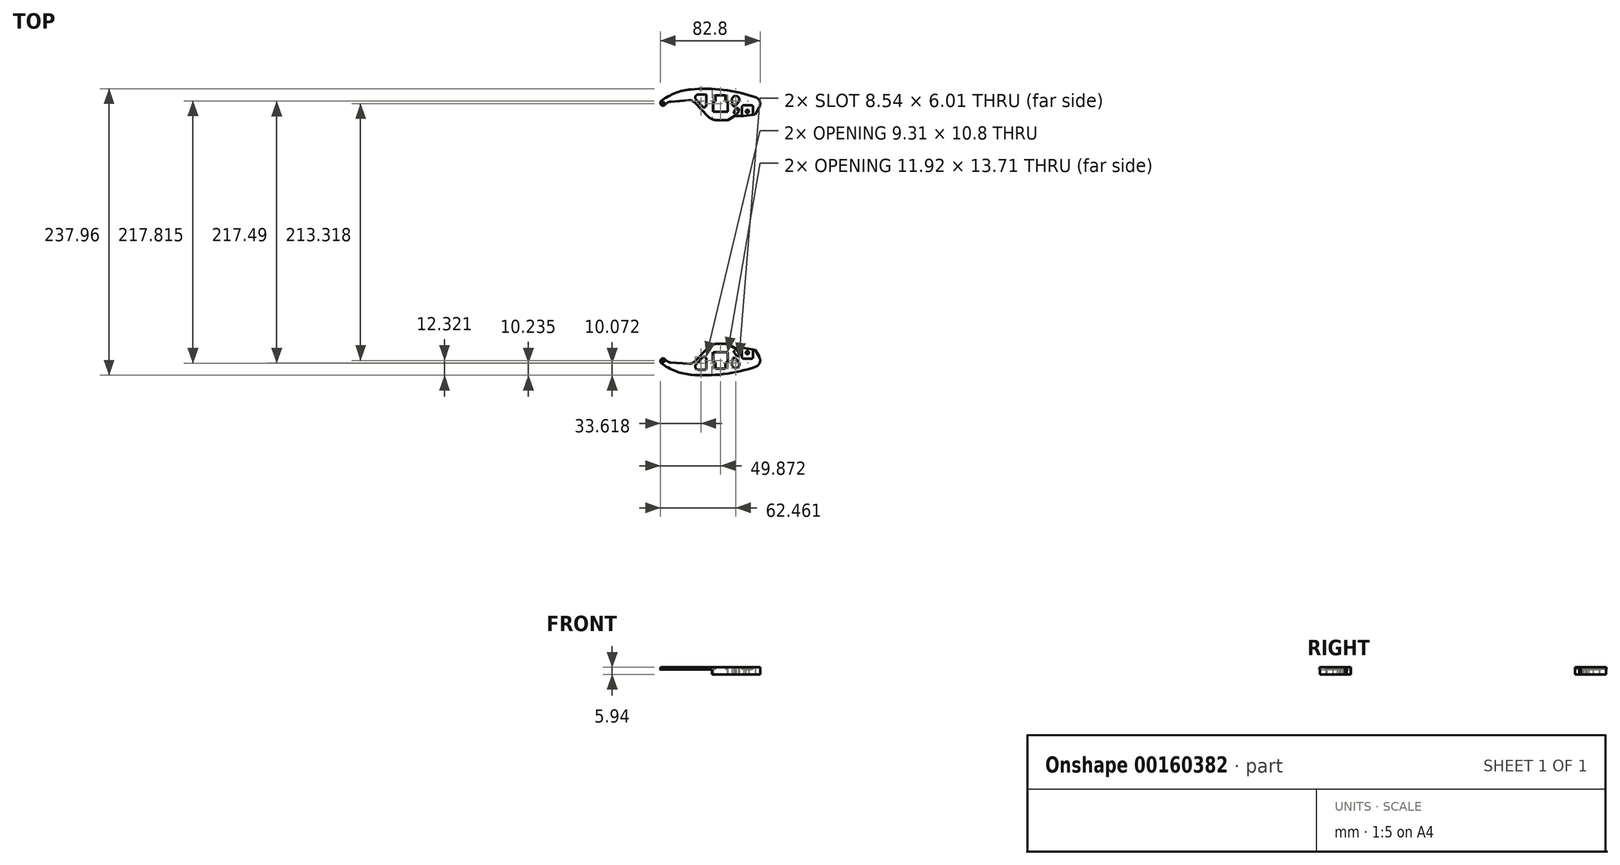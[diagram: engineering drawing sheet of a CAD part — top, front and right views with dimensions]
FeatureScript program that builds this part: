
annotation { "Feature Type Name" : "Feature", "Feature Type Description" : "" }
export const myFeature = defineFeature(function(context is Context, id is Id, definition is map)
    precondition{}
    {
        {
            var Q0;
            Q0=qCreatedBy(makeId("Top.planeOp"),FACE);
            var sketch = newSketch(context, id + "F0", { "sketchPlane" : qUnion([Q0])});
            skLineSegment(sketch, "E0", {"start": v(-38.77, 92.9) * mm, "end": v(-48, 92.9) * mm});
            skArc(sketch, "E1", {"start": v(-48, 92.9) * mm, "mid": v(-51.77, 93.67) * mm, "end": v(-54.94, 95.84) * mm});
            skLineSegment(sketch, "E2", {"start": v(-54.94, 95.84) * mm, "end": v(-66.16, 107.4) * mm});
            skArc(sketch, "E3", {"start": v(-66.16, 107.4) * mm, "mid": v(-68.67, 109.05) * mm, "end": v(-71.65, 109.47) * mm});
            skLineSegment(sketch, "E4", {"start": v(-71.65, 109.47) * mm, "end": v(-86.34, 108.3) * mm});
            skArc(sketch, "E5", {"start": v(-86.34, 108.3) * mm, "mid": v(-88.83, 107.55) * mm, "end": v(-90.8, 105.86) * mm});
            skArc(sketch, "E6", {"start": v(-90.8, 105.86) * mm, "mid": v(-94.13, 105.64) * mm, "end": v(-93.92, 108.96) * mm});
            skArc(sketch, "E7", {"start": v(-69.69, 118.46) * mm, "mid": v(-82.47, 115.43) * mm, "end": v(-93.92, 108.96) * mm});
            skArc(sketch, "E8", {"start": v(-15.82, 111.92) * mm, "mid": v(-42.4, 118.03) * mm, "end": v(-69.69, 118.46) * mm});
            skArc(sketch, "E9", {"start": v(-12.64, 103.92) * mm, "mid": v(-12.39, 108.65) * mm, "end": v(-15.82, 111.92) * mm});
            skLineSegment(sketch, "E10", {"start": v(-12.64, 103.92) * mm, "end": v(-15.88, 97.74) * mm});
            skLineSegment(sketch, "E11", {"start": v(-15.88, 97.74) * mm, "end": v(-25.7, 96.38) * mm});
            skLineSegment(sketch, "E12", {"start": v(-25.7, 96.38) * mm, "end": v(-33.28, 96.38) * mm});
            skLineSegment(sketch, "E13", {"start": v(-33.28, 96.38) * mm, "end": v(-38.77, 92.9) * mm});
            skCircle(sketch, "E14", {"center": v(-32.29, 110) * mm, "radius": 3.05 * mm});
            skCircle(sketch, "E15", {"center": v(-33.62, 105.82) * mm, "radius": 1.35 * mm});
            skLineSegment(sketch, "E16", {"start": v(-35.32, 109.73) * mm, "end": v(-34.96, 105.7) * mm});
            skLineSegment(sketch, "E17", {"start": v(-29.81, 108.23) * mm, "end": v(-32.59, 104.95) * mm});
            skCircle(sketch, "E18", {"center": v(-30.89, 101.86) * mm, "radius": 1.08 * mm});
            skCircle(sketch, "E19", {"center": v(-30.6, 100.02) * mm, "radius": 0.75 * mm});
            skCircle(sketch, "E20", {"center": v(-32.75, 99.4) * mm, "radius": 1.08 * mm});
            skCircle(sketch, "E21", {"center": v(-31.77, 98.94) * mm, "radius": 0.7 * mm});
            skLineSegment(sketch, "E22", {"start": v(-32.97, 98.34) * mm, "end": v(-31.82, 98.25) * mm});
            skLineSegment(sketch, "E23", {"start": v(-31.32, 98.42) * mm, "end": v(-30.1, 99.45) * mm});
            skLineSegment(sketch, "E24", {"start": v(-29.85, 100.12) * mm, "end": v(-29.8, 101.83) * mm});
            skLineSegment(sketch, "E25", {"start": v(-31.73, 102.54) * mm, "end": v(-33.61, 100.05) * mm});
            skLineSegment(sketch, "E26.bottom", {"start": v(-38.95, 108.35) * mm, "end": v(-50.87, 108.35) * mm});
            skLineSegment(sketch, "E26.top", {"start": v(-38.95, 99.8) * mm, "end": v(-50.87, 99.8) * mm});
            skLineSegment(sketch, "E26.left", {"start": v(-38.95, 108.35) * mm, "end": v(-38.95, 99.8) * mm});
            skLineSegment(sketch, "E26.right", {"start": v(-50.87, 108.35) * mm, "end": v(-50.87, 99.8) * mm});
            skLineSegment(sketch, "E27.bottom", {"start": v(-40.93, 113.51) * mm, "end": v(-49.08, 113.51) * mm});
            skLineSegment(sketch, "E27.top", {"start": v(-40.93, 108.35) * mm, "end": v(-49.08, 108.35) * mm});
            skLineSegment(sketch, "E27.left", {"start": v(-40.93, 113.51) * mm, "end": v(-40.93, 108.35) * mm});
            skLineSegment(sketch, "E27.right", {"start": v(-49.08, 113.51) * mm, "end": v(-49.08, 108.35) * mm});
            skLineSegment(sketch, "E28", {"start": v(-56.5, 113.04) * mm, "end": v(-56.5, 105.52) * mm});
            skLineSegment(sketch, "E29", {"start": v(-56.84, 104.67) * mm, "end": v(-57.51, 103.92) * mm});
            skLineSegment(sketch, "E30", {"start": v(-59.38, 103.9) * mm, "end": v(-64.82, 109.63) * mm});
            skLineSegment(sketch, "E31", {"start": v(-57.78, 114.3) * mm, "end": v(-63.2, 114.3) * mm});
            skArc(sketch, "E32", {"start": v(-63.2, 114.3) * mm, "mid": v(-65.67, 112.55) * mm, "end": v(-64.82, 109.63) * mm});
            skPoint(sketch, "E33.visualSharp", {"position": v(-56.5, 114.3) * mm});
            skArc(sketch, "E33.filletArc", {"start": v(-56.5, 113.04) * mm, "mid": v(-56.88, 113.94) * mm, "end": v(-57.78, 114.3) * mm});
            skPoint(sketch, "E34.visualSharp", {"position": v(-58.43, 102.9) * mm});
            skArc(sketch, "E34.filletArc", {"start": v(-59.38, 103.9) * mm, "mid": v(-58.44, 103.5) * mm, "end": v(-57.51, 103.92) * mm});
            skPoint(sketch, "E35.visualSharp", {"position": v(-56.5, 105.04) * mm});
            skArc(sketch, "E35.filletArc", {"start": v(-56.84, 104.67) * mm, "mid": v(-56.6, 105.07) * mm, "end": v(-56.5, 105.52) * mm});
            skCircle(sketch, "E36", {"center": v(-92.57, 107.2) * mm, "radius": 0.95 * mm});
            skCircle(sketch, "E37", {"center": v(-22.58, 100.2) * mm, "radius": 1.27 * mm});
            skSolve(sketch);
        }
        {
            var Q0;
            Q0 = qSketchRegion(id + "F0", true);
            extrude(context, id + "F1", {"entities" : qUnion([Q0]), "depth" : 1.98 * mm});
        }
        {
            var Q0;
            Q0=makeQuery(id+"F1.opExtrude","CAP_FACE",FACE,{"disambiguationData":[OSD([sQuery(id+"F0.wireOp",EDGE,"E0"),sQuery(id+"F0.wireOp",EDGE,"E1"),sQuery(id+"F0.wireOp",EDGE,"E2"),sQuery(id+"F0.wireOp",EDGE,"E3"),sQuery(id+"F0.wireOp",EDGE,"E4"),sQuery(id+"F0.wireOp",EDGE,"E5"),sQuery(id+"F0.wireOp",EDGE,"E6"),sQuery(id+"F0.wireOp",EDGE,"E7"),sQuery(id+"F0.wireOp",EDGE,"E8"),sQuery(id+"F0.wireOp",EDGE,"E9"),sQuery(id+"F0.wireOp",EDGE,"E10"),sQuery(id+"F0.wireOp",EDGE,"E11"),sQuery(id+"F0.wireOp",EDGE,"E12"),sQuery(id+"F0.wireOp",EDGE,"E13"),sQuery(id+"F0.wireOp",EDGE,"E14"),sQuery(id+"F0.wireOp",EDGE,"E15"),sQuery(id+"F0.wireOp",EDGE,"E16"),sQuery(id+"F0.wireOp",EDGE,"E17"),sQuery(id+"F0.wireOp",EDGE,"E18"),sQuery(id+"F0.wireOp",EDGE,"E19"),sQuery(id+"F0.wireOp",EDGE,"E20"),sQuery(id+"F0.wireOp",EDGE,"E21"),sQuery(id+"F0.wireOp",EDGE,"E22"),sQuery(id+"F0.wireOp",EDGE,"E23"),sQuery(id+"F0.wireOp",EDGE,"E24"),sQuery(id+"F0.wireOp",EDGE,"E25"),sQuery(id+"F0.wireOp",EDGE,"E26.bottom"),sQuery(id+"F0.wireOp",EDGE,"E26.top"),sQuery(id+"F0.wireOp",EDGE,"E26.left"),sQuery(id+"F0.wireOp",EDGE,"E26.right"),sQuery(id+"F0.wireOp",EDGE,"E27.bottom"),sQuery(id+"F0.wireOp",EDGE,"E27.left"),sQuery(id+"F0.wireOp",EDGE,"E27.right"),sQuery(id+"F0.wireOp",EDGE,"E28"),sQuery(id+"F0.wireOp",EDGE,"E29"),sQuery(id+"F0.wireOp",EDGE,"E30"),sQuery(id+"F0.wireOp",EDGE,"E31"),sQuery(id+"F0.wireOp",EDGE,"E32"),sQuery(id+"F0.wireOp",EDGE,"E33.filletArc"),sQuery(id+"F0.wireOp",EDGE,"E34.filletArc"),sQuery(id+"F0.wireOp",EDGE,"E35.filletArc"),sQuery(id+"F0.wireOp",EDGE,"E36"),sQuery(id+"F0.wireOp",EDGE,"E37")])],"isStart":true});
            var sketch = newSketch(context, id + "F2", { "sketchPlane" : qUnion([Q0])});
            skArc(sketch, "E38.0", {"start": v(-30.13, -107.86) * mm, "mid": v(-31.26, -112.87) * mm, "end": v(-35.32, -109.73) * mm});
            skLineSegment(sketch, "E38.1", {"start": v(-30.13, -107.86) * mm, "end": v(-32.59, -104.95) * mm});
            skArc(sketch, "E38.2", {"start": v(-34.96, -105.7) * mm, "mid": v(-34.02, -104.54) * mm, "end": v(-32.59, -104.95) * mm});
            skLineSegment(sketch, "E38.3", {"start": v(-35.32, -109.73) * mm, "end": v(-34.96, -105.7) * mm});
            skLineSegment(sketch, "E38.4", {"start": v(-31.77, -102.48) * mm, "end": v(-33.61, -100.05) * mm});
            skArc(sketch, "E38.5", {"start": v(-29.8, -101.83) * mm, "mid": v(-30.55, -102.88) * mm, "end": v(-31.77, -102.48) * mm});
            skLineSegment(sketch, "E38.6", {"start": v(-29.85, -100.12) * mm, "end": v(-29.8, -101.83) * mm});
            skPoint(sketch, "E38.7", {"position": v(-29.85, -100.12) * mm});
            skPoint(sketch, "E38.8", {"position": v(-31.32, -98.42) * mm});
            skArc(sketch, "E38.9", {"start": v(-30.1, -99.45) * mm, "mid": v(-29.9, -99.75) * mm, "end": v(-29.85, -100.12) * mm});
            skLineSegment(sketch, "E38.10", {"start": v(-31.32, -98.42) * mm, "end": v(-30.1, -99.45) * mm});
            skArc(sketch, "E38.11", {"start": v(-31.82, -98.25) * mm, "mid": v(-31.55, -98.29) * mm, "end": v(-31.32, -98.42) * mm});
            skLineSegment(sketch, "E38.12", {"start": v(-32.7, -98.32) * mm, "end": v(-31.82, -98.25) * mm});
            skArc(sketch, "E38.13", {"start": v(-33.61, -100.05) * mm, "mid": v(-33.7, -98.89) * mm, "end": v(-32.7, -98.32) * mm});
            skCircle(sketch, "E38.14", {"center": v(-22.58, -100.2) * mm, "radius": 1.27 * mm});
            skLineSegment(sketch, "E38.15", {"start": v(-12.64, -103.92) * mm, "end": v(-15.88, -97.74) * mm});
            skArc(sketch, "E38.16", {"start": v(-12.64, -103.92) * mm, "mid": v(-12.39, -108.65) * mm, "end": v(-15.82, -111.92) * mm});
            skArc(sketch, "E38.17", {"start": v(-15.82, -111.92) * mm, "mid": v(-33.6, -116.65) * mm, "end": v(-51.88, -118.83) * mm});
            skLineSegment(sketch, "E38.18", {"start": v(-25.7, -96.38) * mm, "end": v(-33.28, -96.38) * mm});
            skLineSegment(sketch, "E38.19", {"start": v(-15.88, -97.74) * mm, "end": v(-25.7, -96.38) * mm});
            skLineSegment(sketch, "E38.20", {"start": v(-33.28, -96.38) * mm, "end": v(-38.77, -92.9) * mm});
            skLineSegment(sketch, "E38.21", {"start": v(-38.77, -92.9) * mm, "end": v(-48, -92.9) * mm});
            skLineSegment(sketch, "E39", {"start": v(-55.8, -70.08) * mm, "end": v(-55.8, -80.65) * mm, "construction": true});
            skLineSegment(sketch, "E40", {"start": v(-56.81, -69.9) * mm, "end": v(-56.81, -80.65) * mm, "construction": true});
            skLineSegment(sketch, "E41.bottom", {"start": v(-38.95, -99.8) * mm, "end": v(-50.87, -99.8) * mm});
            skLineSegment(sketch, "E41.top", {"start": v(-38.95, -113.51) * mm, "end": v(-50.87, -113.51) * mm});
            skLineSegment(sketch, "E41.left", {"start": v(-38.95, -99.8) * mm, "end": v(-38.95, -113.51) * mm});
            skLineSegment(sketch, "E41.right", {"start": v(-50.87, -99.8) * mm, "end": v(-50.87, -113.51) * mm});
            skLineSegment(sketch, "E42", {"start": v(-51.88, -118.83) * mm, "end": v(-51.88, -93.72) * mm});
            skPoint(sketch, "E43.orphan", {"position": v(-69.69, -118.46) * mm});
            skArc(sketch, "E44", {"start": v(-48, -92.9) * mm, "mid": v(-49.98, -93.1) * mm, "end": v(-51.88, -93.72) * mm});
            skSolve(sketch);
        }
        {
            var Q0;
            Q0 = qSketchRegion(id + "F2", true);
            extrude(context, id + "F3", {"entities" : qUnion([Q0]), "operationType" : NewBodyOperationType.ADD, "depth" : 1.98 * mm * 2});
        }
        {
            var Q0;
            Q0=makeQuery(id+"F1.opExtrude","CAP_FACE",FACE,{"disambiguationData":[OSD([sQuery(id+"F0.wireOp",EDGE,"E0"),sQuery(id+"F0.wireOp",EDGE,"E1"),sQuery(id+"F0.wireOp",EDGE,"E2"),sQuery(id+"F0.wireOp",EDGE,"E3"),sQuery(id+"F0.wireOp",EDGE,"E4"),sQuery(id+"F0.wireOp",EDGE,"E5"),sQuery(id+"F0.wireOp",EDGE,"E6"),sQuery(id+"F0.wireOp",EDGE,"E7"),sQuery(id+"F0.wireOp",EDGE,"E8"),sQuery(id+"F0.wireOp",EDGE,"E9"),sQuery(id+"F0.wireOp",EDGE,"E10"),sQuery(id+"F0.wireOp",EDGE,"E11"),sQuery(id+"F0.wireOp",EDGE,"E12"),sQuery(id+"F0.wireOp",EDGE,"E13"),sQuery(id+"F0.wireOp",EDGE,"E14"),sQuery(id+"F0.wireOp",EDGE,"E15"),sQuery(id+"F0.wireOp",EDGE,"E16"),sQuery(id+"F0.wireOp",EDGE,"E17"),sQuery(id+"F0.wireOp",EDGE,"E18"),sQuery(id+"F0.wireOp",EDGE,"E19"),sQuery(id+"F0.wireOp",EDGE,"E20"),sQuery(id+"F0.wireOp",EDGE,"E21"),sQuery(id+"F0.wireOp",EDGE,"E22"),sQuery(id+"F0.wireOp",EDGE,"E23"),sQuery(id+"F0.wireOp",EDGE,"E24"),sQuery(id+"F0.wireOp",EDGE,"E25"),sQuery(id+"F0.wireOp",EDGE,"E26.bottom"),sQuery(id+"F0.wireOp",EDGE,"E26.top"),sQuery(id+"F0.wireOp",EDGE,"E26.left"),sQuery(id+"F0.wireOp",EDGE,"E26.right"),sQuery(id+"F0.wireOp",EDGE,"E27.bottom"),sQuery(id+"F0.wireOp",EDGE,"E27.left"),sQuery(id+"F0.wireOp",EDGE,"E27.right"),sQuery(id+"F0.wireOp",EDGE,"E28"),sQuery(id+"F0.wireOp",EDGE,"E29"),sQuery(id+"F0.wireOp",EDGE,"E30"),sQuery(id+"F0.wireOp",EDGE,"E31"),sQuery(id+"F0.wireOp",EDGE,"E32"),sQuery(id+"F0.wireOp",EDGE,"E33.filletArc"),sQuery(id+"F0.wireOp",EDGE,"E34.filletArc"),sQuery(id+"F0.wireOp",EDGE,"E35.filletArc"),sQuery(id+"F0.wireOp",EDGE,"E36"),sQuery(id+"F0.wireOp",EDGE,"E37")])],"isStart":false});
            var sketch = newSketch(context, id + "F4", { "sketchPlane" : qUnion([Q0])});
            skLineSegment(sketch, "E45.bottom", {"start": v(-27.06, 96.38) * mm, "end": v(-25.7, 96.38) * mm});
            skLineSegment(sketch, "E45.top", {"start": v(-25.8, 105.18) * mm, "end": v(-19.19, 105.18) * mm});
            skLineSegment(sketch, "E45.left", {"start": v(-27.06, 96.38) * mm, "end": v(-27.06, 103.91) * mm});
            skLineSegment(sketch, "E45.right", {"start": v(-17.92, 97.46) * mm, "end": v(-17.92, 103.91) * mm});
            skLineSegment(sketch, "E46.0", {"start": v(-17.92, 97.46) * mm, "end": v(-25.7, 96.38) * mm});
            skPoint(sketch, "E47.orphan", {"position": v(-15.88, 97.74) * mm});
            skPoint(sketch, "E48.visualSharp", {"position": v(-27.06, 105.18) * mm});
            skArc(sketch, "E48.filletArc", {"start": v(-25.8, 105.18) * mm, "mid": v(-26.69, 104.8) * mm, "end": v(-27.06, 103.91) * mm});
            skPoint(sketch, "E49.visualSharp", {"position": v(-17.92, 105.18) * mm});
            skArc(sketch, "E49.filletArc", {"start": v(-17.92, 103.91) * mm, "mid": v(-18.3, 104.8) * mm, "end": v(-19.19, 105.18) * mm});
            skSolve(sketch);
        }
        {
            var Q0;
            Q0 = qSketchRegion(id + "F4", true);
            extrude(context, id + "F5", {"entities" : qUnion([Q0]), "operationType" : NewBodyOperationType.REMOVE, "oppositeDirection" : true, "depth" : 1.98 * mm});
        }
        {
            var Q0;
            Q0=makeQuery(id+"F1.opExtrude","SWEPT_BODY",BODY,{"disambiguationData":[OSD([sQuery(id+"F0.wireOp",EDGE,"E0"),sQuery(id+"F0.wireOp",EDGE,"E1"),sQuery(id+"F0.wireOp",EDGE,"E2"),sQuery(id+"F0.wireOp",EDGE,"E3"),sQuery(id+"F0.wireOp",EDGE,"E4"),sQuery(id+"F0.wireOp",EDGE,"E5"),sQuery(id+"F0.wireOp",EDGE,"E6"),sQuery(id+"F0.wireOp",EDGE,"E7"),sQuery(id+"F0.wireOp",EDGE,"E8"),sQuery(id+"F0.wireOp",EDGE,"E9"),sQuery(id+"F0.wireOp",EDGE,"E10"),sQuery(id+"F0.wireOp",EDGE,"E11"),sQuery(id+"F0.wireOp",EDGE,"E12"),sQuery(id+"F0.wireOp",EDGE,"E13"),sQuery(id+"F0.wireOp",EDGE,"E14"),sQuery(id+"F0.wireOp",EDGE,"E15"),sQuery(id+"F0.wireOp",EDGE,"E16"),sQuery(id+"F0.wireOp",EDGE,"E17"),sQuery(id+"F0.wireOp",EDGE,"E18"),sQuery(id+"F0.wireOp",EDGE,"E19"),sQuery(id+"F0.wireOp",EDGE,"E20"),sQuery(id+"F0.wireOp",EDGE,"E21"),sQuery(id+"F0.wireOp",EDGE,"E22"),sQuery(id+"F0.wireOp",EDGE,"E23"),sQuery(id+"F0.wireOp",EDGE,"E24"),sQuery(id+"F0.wireOp",EDGE,"E25"),sQuery(id+"F0.wireOp",EDGE,"E26.bottom"),sQuery(id+"F0.wireOp",EDGE,"E26.top"),sQuery(id+"F0.wireOp",EDGE,"E26.left"),sQuery(id+"F0.wireOp",EDGE,"E26.right"),sQuery(id+"F0.wireOp",EDGE,"E27.bottom"),sQuery(id+"F0.wireOp",EDGE,"E27.left"),sQuery(id+"F0.wireOp",EDGE,"E27.right"),sQuery(id+"F0.wireOp",EDGE,"E28"),sQuery(id+"F0.wireOp",EDGE,"E29"),sQuery(id+"F0.wireOp",EDGE,"E30"),sQuery(id+"F0.wireOp",EDGE,"E31"),sQuery(id+"F0.wireOp",EDGE,"E32"),sQuery(id+"F0.wireOp",EDGE,"E33.filletArc"),sQuery(id+"F0.wireOp",EDGE,"E34.filletArc"),sQuery(id+"F0.wireOp",EDGE,"E35.filletArc"),sQuery(id+"F0.wireOp",EDGE,"E36"),sQuery(id+"F0.wireOp",EDGE,"E37")])]});
            var Q1;
            Q1=qCreatedBy(makeId("Front.planeOp"),FACE);
            mirror(context, id + "F6", {"entities" : qUnion([Q0]), "mirrorPlane" : qUnion([Q1])});
        }
    });
